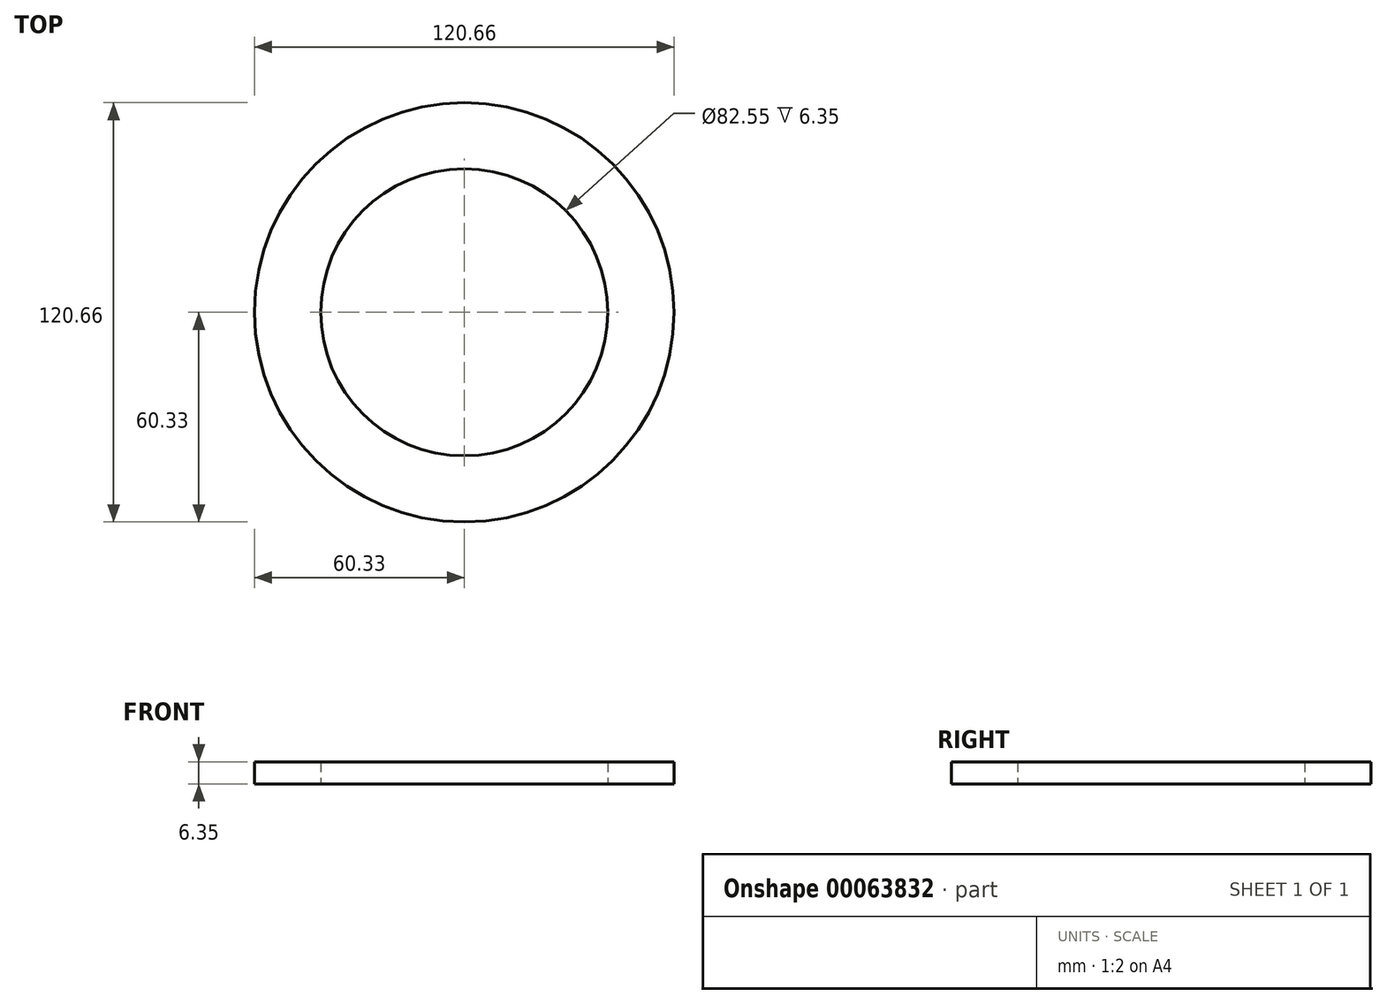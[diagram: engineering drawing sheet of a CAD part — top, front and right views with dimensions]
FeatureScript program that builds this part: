
annotation { "Feature Type Name" : "Feature", "Feature Type Description" : "" }
export const myFeature = defineFeature(function(context is Context, id is Id, definition is map)
    precondition{}
    {
        {
            var Q0;
            Q0=qCreatedBy(makeId("Top.planeOp"),FACE);
            var sketch = newSketch(context, id + "F0", { "sketchPlane" : qUnion([Q0])});
            skCircle(sketch, "E0", {"center": v(0, 0) * mm, "radius": 60.33 * mm});
            skCircle(sketch, "E1", {"center": v(0, 0) * mm, "radius": 41.28 * mm});
            skSolve(sketch);
        }
        {
            var Q0;
            Q0=qSketchRegion(id+"F0",true);
            extrude(context, id + "F1", {"entities" : qUnion([Q0]), "depth" : 6.35 * mm});
        }
    });
